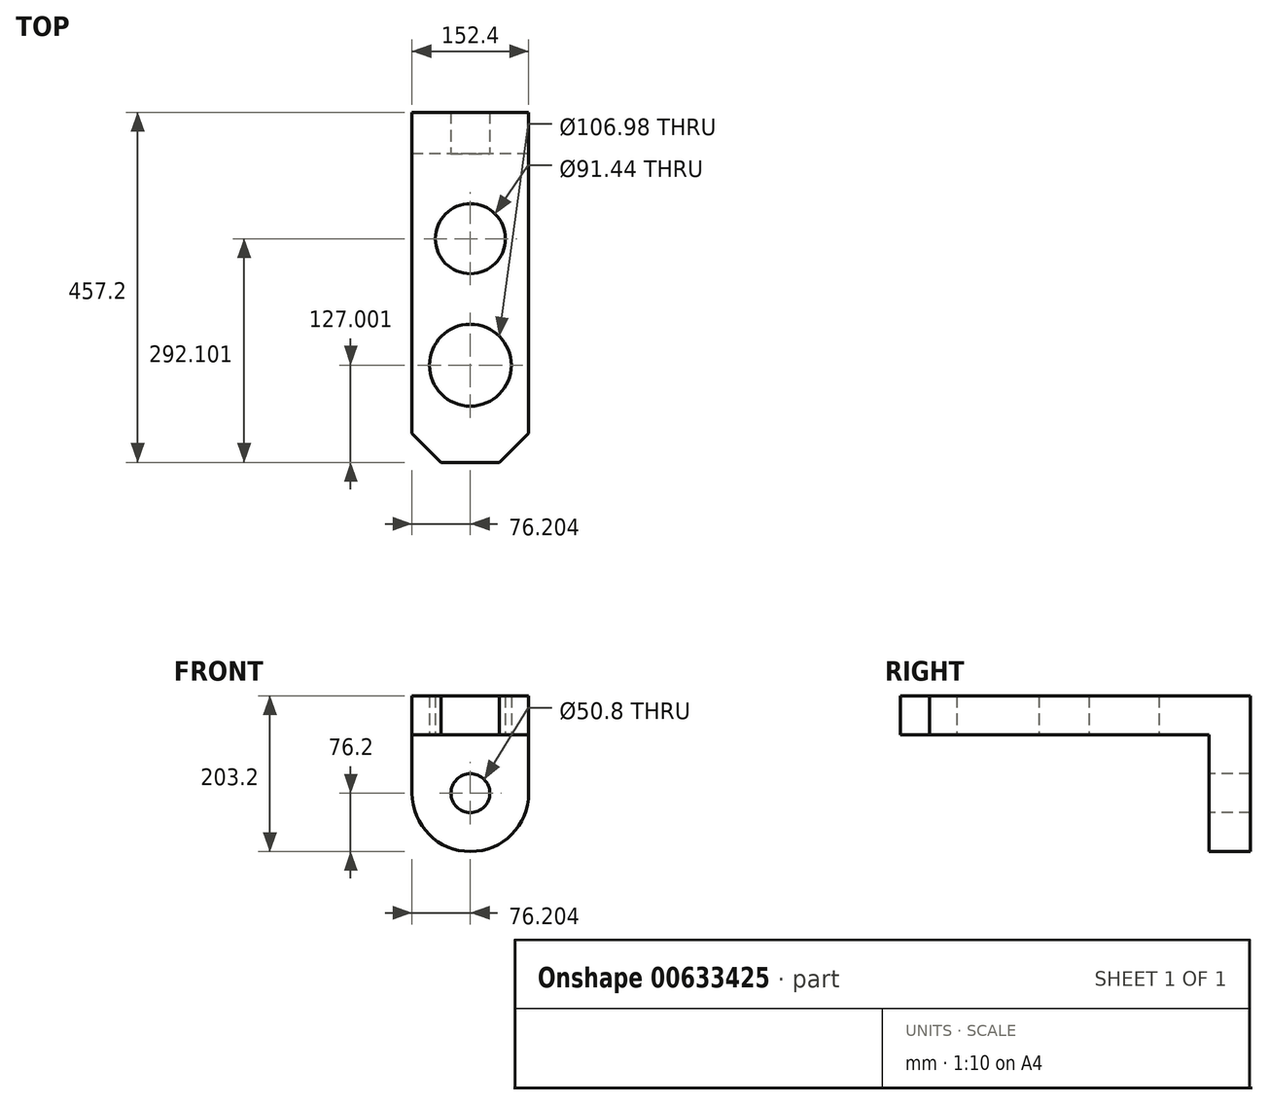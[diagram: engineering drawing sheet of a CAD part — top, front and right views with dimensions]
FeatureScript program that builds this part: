
annotation { "Feature Type Name" : "Feature", "Feature Type Description" : "" }
export const myFeature = defineFeature(function(context is Context, id is Id, definition is map)
    precondition{}
    {
        {
            var Q0;
            Q0=qCreatedBy(makeId("Top.planeOp"),FACE);
            var sketch = newSketch(context, id + "F0", { "sketchPlane" : qUnion([Q0])});
            skLineSegment(sketch, "E0.bottom", {"start": v(-36.36, 445.08) * mm, "end": v(116.04, 445.08) * mm});
            skLineSegment(sketch, "E0.top", {"start": v(-36.36, -12.12) * mm, "end": v(116.04, -12.12) * mm});
            skLineSegment(sketch, "E0.left", {"start": v(-36.36, 445.08) * mm, "end": v(-36.36, -12.12) * mm});
            skLineSegment(sketch, "E0.right", {"start": v(116.04, 445.08) * mm, "end": v(116.04, -12.12) * mm});
            skSolve(sketch);
        }
        {
            var Q0;
            Q0=makeQuery(id+"F0.imprint","IMPRINT",FACE,{"disambiguationData":[TD([[makeQuery(id+"F0.imprint","IMPRINT",EDGE,{"derivedFrom":sQuery(id+"F0.wireOp",EDGE,"E0.bottom")}),-1.0]])]});
            extrude(context, id + "F1", {"entities" : qUnion([Q0]), "depth" : 50.8 * mm, "offsetDistance" : 25.4 * mm});
        }
        {
            var Q0;
            Q0=makeQuery(id+"F1.opExtrude","CAP_FACE",FACE,{"disambiguationData":[OSD([sQuery(id+"F0.wireOp",EDGE,"E0.bottom"),sQuery(id+"F0.wireOp",EDGE,"E0.top"),sQuery(id+"F0.wireOp",EDGE,"E0.left"),sQuery(id+"F0.wireOp",EDGE,"E0.right")])],"isStart":true});
            var sketch = newSketch(context, id + "F2", { "sketchPlane" : qUnion([Q0])});
            skLineSegment(sketch, "E1.bottom", {"start": v(116.04, -445.08) * mm, "end": v(-36.36, -445.08) * mm});
            skLineSegment(sketch, "E1.top", {"start": v(116.04, -390.67) * mm, "end": v(-36.36, -390.67) * mm});
            skLineSegment(sketch, "E1.left", {"start": v(116.04, -445.08) * mm, "end": v(116.04, -390.67) * mm});
            skLineSegment(sketch, "E1.right", {"start": v(-36.36, -445.08) * mm, "end": v(-36.36, -390.67) * mm});
            skSolve(sketch);
        }
        {
            var Q0;
            Q0=makeQuery(id+"F2.imprint","IMPRINT",FACE,{"disambiguationData":[TD([[makeQuery(id+"F2.imprint","IMPRINT",EDGE,{"derivedFrom":sQuery(id+"F2.wireOp",EDGE,"E1.bottom")}),1.0]])]});
            extrude(context, id + "F3", {"entities" : qUnion([Q0]), "operationType" : NewBodyOperationType.ADD, "depth" : 152.4 * mm, "offsetDistance" : 25.4 * mm});
        }
        {
            var Q0;
            Q0=makeQuery(id+"F3.opExtrude","CAP_EDGE",EDGE,{"disambiguationData":[OSD([sQuery(id+"F2.wireOp",EDGE,"E1.left")])],"isStart":false});
            var Q1;
            Q1=makeQuery(id+"F3.opExtrude","CAP_EDGE",EDGE,{"disambiguationData":[OSD([sQuery(id+"F2.wireOp",EDGE,"E1.right")])],"isStart":false});
            fillet(context, id + "F4", {"entities" : qUnion([Q0, Q1]), "radius" : 76.2 * mm, "tangentPropagation" : true, "allowEdgeOverflow" : false});
        }
        {
            var Q0;
            {var subQ0=sQuery(id+"F2.wireOp",EDGE,"E1.top");Q0=makeQuery(id+"F2.imprint","IMPRINT",FACE,{"disambiguationData":[TD([[makeQuery(id+"F2.imprint","IMPRINT",EDGE,{"derivedFrom":subQ0}),-1.0]])]});}
            var sketch = newSketch(context, id + "F5", { "sketchPlane" : qUnion([Q0])});
            skCircle(sketch, "E2", {"center": v(39.84, -279.98) * mm, "radius": 45.72 * mm});
            skCircle(sketch, "E3", {"center": v(39.84, -114.88) * mm, "radius": 53.49 * mm});
            skSolve(sketch);
        }
        {
            var Q0;
            Q0 = qSketchRegion(id + "F5", true);
            extrude(context, id + "F6", {"entities" : qUnion([Q0]), "operationType" : NewBodyOperationType.REMOVE, "endBound" : BoundingType.THROUGH_ALL, "oppositeDirection" : true, "depth" : 25.4 * mm, "offsetDistance" : 25.4 * mm});
        }
        {
            var Q0;
            Q0=makeQuery(id+"F3.opExtrude","SWEPT_FACE",FACE,{"disambiguationData":[OSD([sQuery(id+"F2.wireOp",EDGE,"E1.top")])]});
            var sketch = newSketch(context, id + "F7", { "sketchPlane" : qUnion([Q0])});
            skCircle(sketch, "E4", {"center": v(39.84, -76.2) * mm, "radius": 25.4 * mm});
            skSolve(sketch);
        }
        {
            var Q0;
            Q0 = qSketchRegion(id + "F7", true);
            extrude(context, id + "F8", {"entities" : qUnion([Q0]), "operationType" : NewBodyOperationType.REMOVE, "endBound" : BoundingType.THROUGH_ALL, "oppositeDirection" : true, "depth" : 25.4 * mm, "offsetDistance" : 25.4 * mm});
        }
        {
            var Q0;
            Q0=makeQuery(id+"F1.opExtrude","SWEPT_EDGE",EDGE,{"disambiguationData":[OSD([sQuery(id+"F0.wireOp",EDGE,"E0.top"),sQuery(id+"F0.wireOp",EDGE,"E0.right")])]});
            var Q1;
            Q1=makeQuery(id+"F1.opExtrude","SWEPT_EDGE",EDGE,{"disambiguationData":[OSD([sQuery(id+"F0.wireOp",EDGE,"E0.top"),sQuery(id+"F0.wireOp",EDGE,"E0.left")])]});
            chamfer(context, id + "F9", {"entities" : qUnion([Q0, Q1]), "width" : 38.1 * mm, "tangentPropagation" : true});
        }
    });
